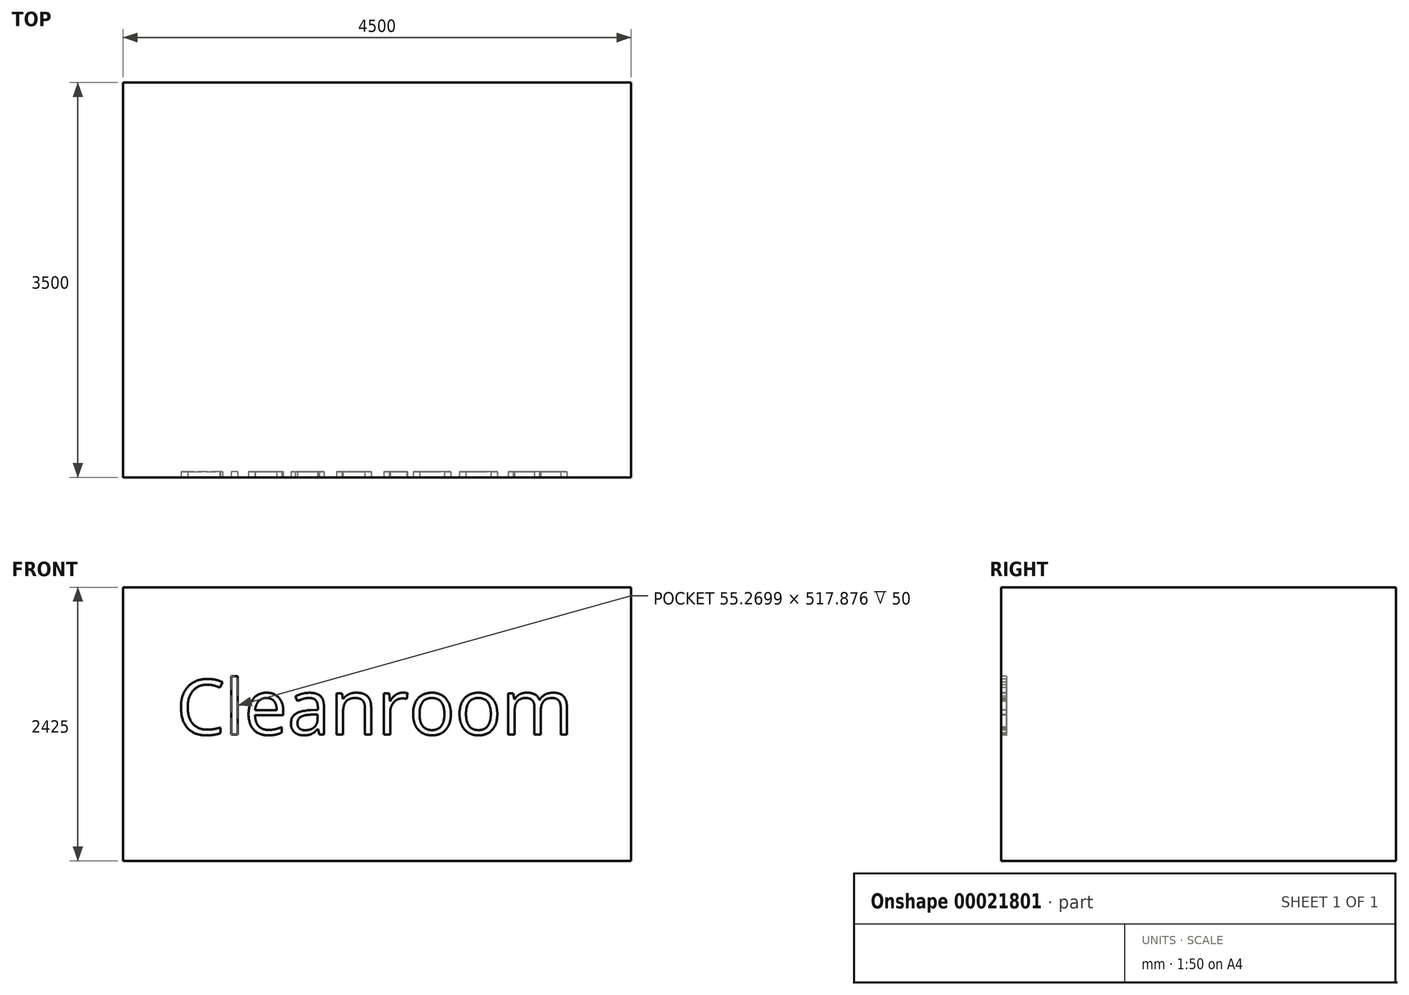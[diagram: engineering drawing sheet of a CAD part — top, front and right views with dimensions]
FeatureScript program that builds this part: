
annotation { "Feature Type Name" : "Feature", "Feature Type Description" : "" }
export const myFeature = defineFeature(function(context is Context, id is Id, definition is map)
    precondition{}
    {
        {
            var Q0;
            Q0=qCreatedBy(makeId("Top.planeOp"),FACE);
            var sketch = newSketch(context, id + "F0", { "sketchPlane" : qUnion([Q0])});
            skLineSegment(sketch, "E0.bottom", {"start": v(0, 0) * mm, "end": v(4500, 0) * mm});
            skLineSegment(sketch, "E0.top", {"start": v(0, 3500) * mm, "end": v(4500, 3500) * mm});
            skLineSegment(sketch, "E0.left", {"start": v(0, 0) * mm, "end": v(0, 3500) * mm});
            skLineSegment(sketch, "E0.right", {"start": v(4500, 0) * mm, "end": v(4500, 3500) * mm});
            skSolve(sketch);
        }
        {
            var Q0;
            Q0=makeQuery(id+"F0.imprint","IMPRINT",FACE,{"disambiguationData":[TD([[makeQuery(id+"F0.imprint","IMPRINT",EDGE,{"derivedFrom":sQuery(id+"F0.wireOp",EDGE,"E0.bottom")}),1.0]])]});
            extrude(context, id + "F1", {"entities" : qUnion([Q0]), "depth" : 2425 * mm});
        }
        {
            var Q0;
            Q0=makeQuery(id+"F1.opExtrude","SWEPT_FACE",FACE,{"disambiguationData":[OSD([sQuery(id+"F0.wireOp",EDGE,"E0.bottom")])]});
            var sketch = newSketch(context, id + "F2", { "sketchPlane" : qUnion([Q0])});
            skText(sketch, "E1", { "text": "Cleanroom", "fontName": "OpenSans-Regular.ttf"});
            const initialGuessF2  = {"E1": [0.4708, 1.1191, 1, 0, 0.49072]};
            skSetInitialGuess(sketch, initialGuessF2);
            skSolve(sketch);
        }
        {
            var Q0;
            Q0 = qSketchRegion(id + "F2", true);
            extrude(context, id + "F3", {"entities" : qUnion([Q0]), "operationType" : NewBodyOperationType.REMOVE, "oppositeDirection" : true, "depth" : 50 * mm});
        }
    });
